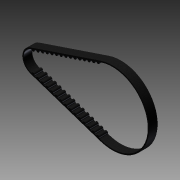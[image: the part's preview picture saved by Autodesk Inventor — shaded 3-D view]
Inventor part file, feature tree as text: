
AUTODESK INVENTOR PART (.ipt)
format: ipt  version: 2012 (Build 160160000, 160)  size: 267,264 bytes
history: native  units: in
note: dims shown in document units (in); Inventor stores cm internally (conversion verified against a paired STEP export)
features: extrude x1, sketch x1
ambient origin geometry x8: Origin, YZ Plane, XZ Plane, XY Plane, X Axis, Y Axis, Z Axis, Center Point
bodies: Solid1 (feature_tree)
feature tree (2):
  extrude  "Extrusion1"  Depth=0.447in
  sketch  "Sketch1"  dims[d0=3.25in d1=0.447in d2=0.5in d4=0.0625in d5=0.024in d7=5.9055in d9=0.204in d10=0.3937in d12=1.0in d14=0.3543in d15=0.0in d16=1.482in d17=0.01in]
